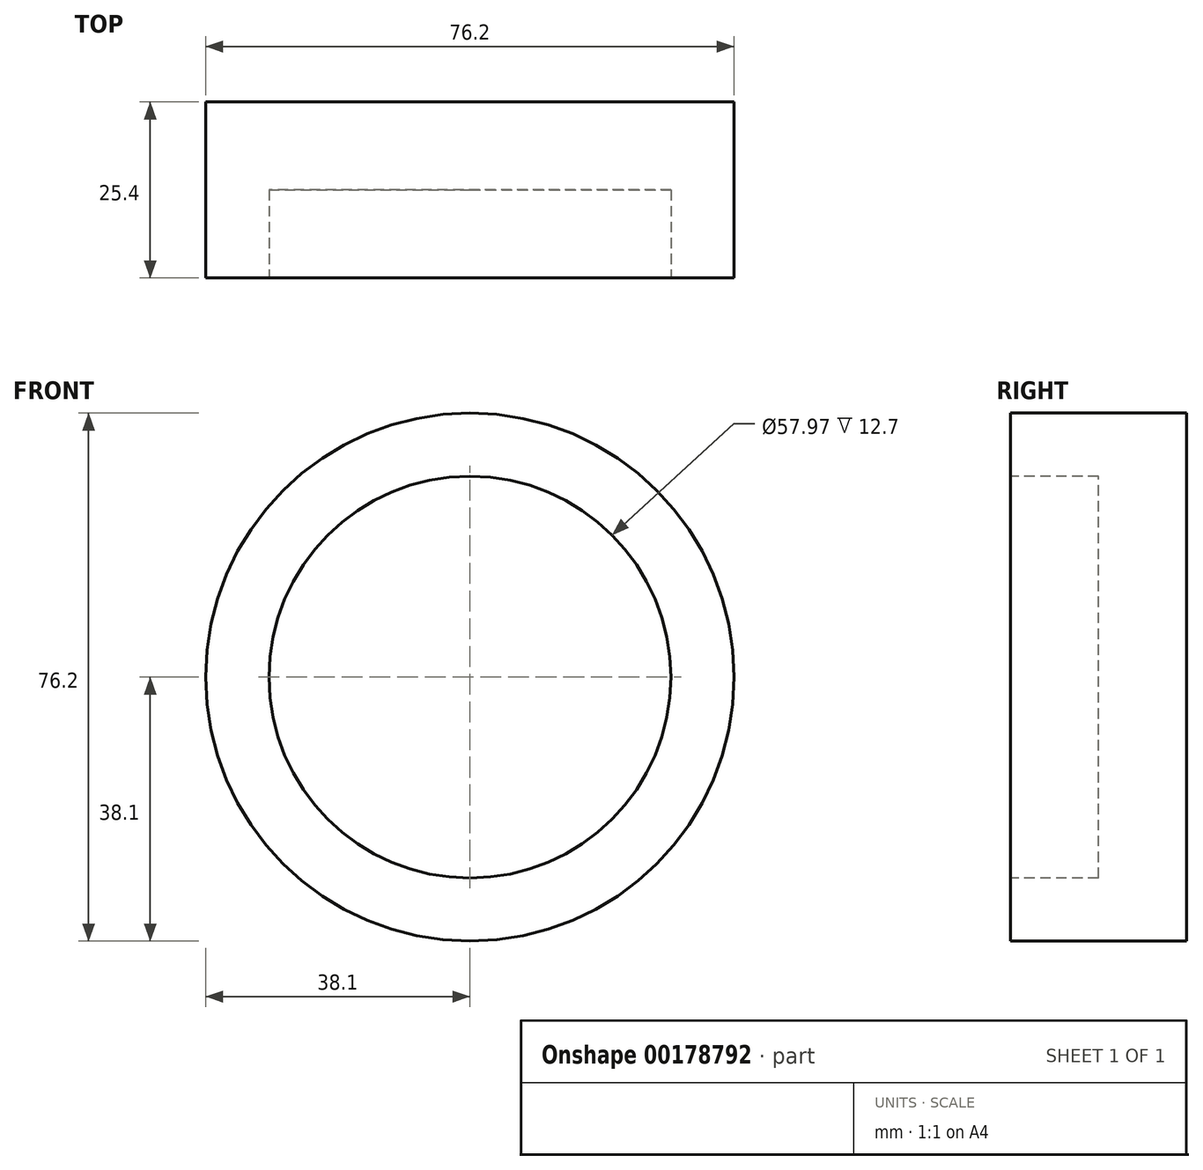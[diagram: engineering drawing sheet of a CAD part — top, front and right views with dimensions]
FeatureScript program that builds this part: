
annotation { "Feature Type Name" : "Feature", "Feature Type Description" : "" }
export const myFeature = defineFeature(function(context is Context, id is Id, definition is map)
    precondition{}
    {
        {
            var Q0;
            Q0=qCreatedBy(makeId("Front.planeOp"),FACE);
            var sketch = newSketch(context, id + "F0", { "sketchPlane" : qUnion([Q0])});
            skCircle(sketch, "E0", {"center": v(0, 0) * mm, "radius": 38.1 * mm});
            skSolve(sketch);
        }
        {
            var Q0;
            Q0=makeQuery(id+"F0.imprint","IMPRINT",FACE,{"disambiguationData":[TD([[makeQuery(id+"F0.imprint","IMPRINT",EDGE,{"derivedFrom":sQuery(id+"F0.wireOp",EDGE,"E0")}),1.0]])]});
            extrude(context, id + "F1", {"entities" : qUnion([Q0]), "depth" : 25.4 * mm});
        }
        {
            var Q0;
            Q0=makeQuery(id+"F1.opExtrude","CAP_FACE",FACE,{"disambiguationData":[OSD([sQuery(id+"F0.wireOp",EDGE,"E0")])],"isStart":false});
            var sketch = newSketch(context, id + "F2", { "sketchPlane" : qUnion([Q0])});
            skCircle(sketch, "E1", {"center": v(0, 0) * mm, "radius": 28.99 * mm});
            skSolve(sketch);
        }
        {
            var Q0;
            Q0=makeQuery(id+"F2.imprint","IMPRINT",FACE,{"disambiguationData":[TD([[makeQuery(id+"F2.imprint","IMPRINT",EDGE,{"derivedFrom":sQuery(id+"F2.wireOp",EDGE,"E1")}),1.0]])]});
            extrude(context, id + "F3", {"entities" : qUnion([Q0]), "operationType" : NewBodyOperationType.REMOVE, "oppositeDirection" : true, "depth" : 12.7 * mm});
        }
        {
            var Q0;
            Q0=makeQuery(id+"F1.opExtrude","CAP_FACE",FACE,{"disambiguationData":[OSD([sQuery(id+"F0.wireOp",EDGE,"E0")])],"isStart":false});
            var sketch = newSketch(context, id + "F4", { "sketchPlane" : qUnion([Q0])});
            skCircle(sketch, "E2", {"center": v(0, 32.67) * mm, "radius": 3.14 * mm});
            skCircle(sketch, "E3.MirrorC", {"center": v(0, -32.67) * mm, "radius": 3.14 * mm});
            skCircle(sketch, "E4", {"center": v(33, 0) * mm, "radius": 2.48 * mm});
            skCircle(sketch, "E5", {"center": v(-34.22, 0) * mm, "radius": 2.57 * mm});
            skSolve(sketch);
        }
        {
            var Q0;
            Q0=sQuery(id+"F4.wireOp",EDGE,"E3.MirrorC");
            var Q1;
            Q1=sQuery(id+"F4.wireOp",EDGE,"E5");
            var Q2;
            Q2=sQuery(id+"F4.wireOp",EDGE,"E4");
            var Q3;
            Q3=sQuery(id+"F4.wireOp",EDGE,"E2");
            extrude(context, id + "F5", {"bodyType" : ToolBodyType.SURFACE, "surfaceEntities" : qUnion([Q0, Q1, Q2, Q3]), "depth" : 76.2 * mm});
        }
    });
